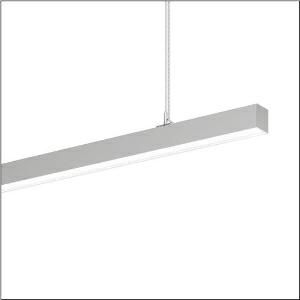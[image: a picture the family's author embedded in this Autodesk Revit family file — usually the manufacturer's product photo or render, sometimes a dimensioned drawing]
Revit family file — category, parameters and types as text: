
# Revit family: silica_r__21_51mx33dc3dsb_c168
name_source: partatom
category: Lighting Fixtures
units: mm (PartAtom-declared; Revit-internal decimal feet)

## family parameters
Cut with Voids When Loaded = No
Host = Face
Light Source = No
Part Type = Normal
Room Calculation Point = No
Round Connector Dimension = Use Diameter
Shared = No

## types (1)
- --- (1 x LED, 14780 lm, 99.5 W, 3000K)
    Apparent Load = 100 VA
    CIE Flux Codes = 78 96 99 55 100
    Color Rendering = 80
    Color Temperature = 3000K
    Default Elevation = 1800 mm
    Description = Silica® 21, office luminaire, primary optical cover: prismatic diffuser, of PMMA, CAT 2 (L<= 3000cd/m²), light emission: direct/indirect distribution, primary light characteristic: symmetric, installation type: suspended mounting, LED, rated luminous flux: 14.780lm, luminous efficacy: 149lm/W, light colour: 830, colour temperature: 3000K, with terminal, 3+2-pole, max. 2.5mm², mains connection: 220..240V, AC, 50/60Hz, rated input power: 99.5W, luminaire housing, of aluminium, metallic grey (RAL 9006), length: 3.004mm, width: 53mm, height: 53mm, protection rating (complete): IP20, insulation class (complete): insulation class I (protective earthing), certification: CE, permissible operating ambient temperature: 0..+35°C, standard: EN 50419, packaging unit: 1 piece
    Height = 53 mm
    Lamp = 1 x LED
    Lamp Light Flux = 14780 lm
    Lamp Power = 99.5 W
    Lamp count = 1
    Length = 3004 mm
    Luminous efficacy = 149 lm/W
    Manufacturer = Siteco
    ModVariant = No
    Model = 51MX33DC3DSB
    Mounting Place = Ceiling
    Mounting Type = Pendant
    Number of Poles = 1
    OnlyDefault = Yes
    Power Factor = 1
    Product Name = Silica® 21
    Product group = office luminaire | ceiling pendant
    ProductGroupID = 902
    Protection Class = Protection class I
    Protection Degree = IP 20
    RLX_Detail_Level = 1
    RLX_Emergency_Light_Flux = 0 lm
    RLX_Emergency_Type = 0
    RLX_Emergency_Type_DB = No
    RlxData = <blob elided: 23425 chars, md5=34165348>
    Socket = socket
    Standby Power = 0 W
    System Light Flux = 14780 lm
    System Power = 100 W
    Type Comments = factory setting: luminous flux: 100 % | dim-lin: 254 | 345 mA
    Type Image = l_1335864.jpg
    URL = http://relux.com
    VarID = @adj_087629
    Voltage = 0 V
    Weight = 0.00 kg
    Width = 53 mm

## geometry (parser evidence)
native form markers: Blend x4, Sweep x13
no freeform markers — native parametric forms only
